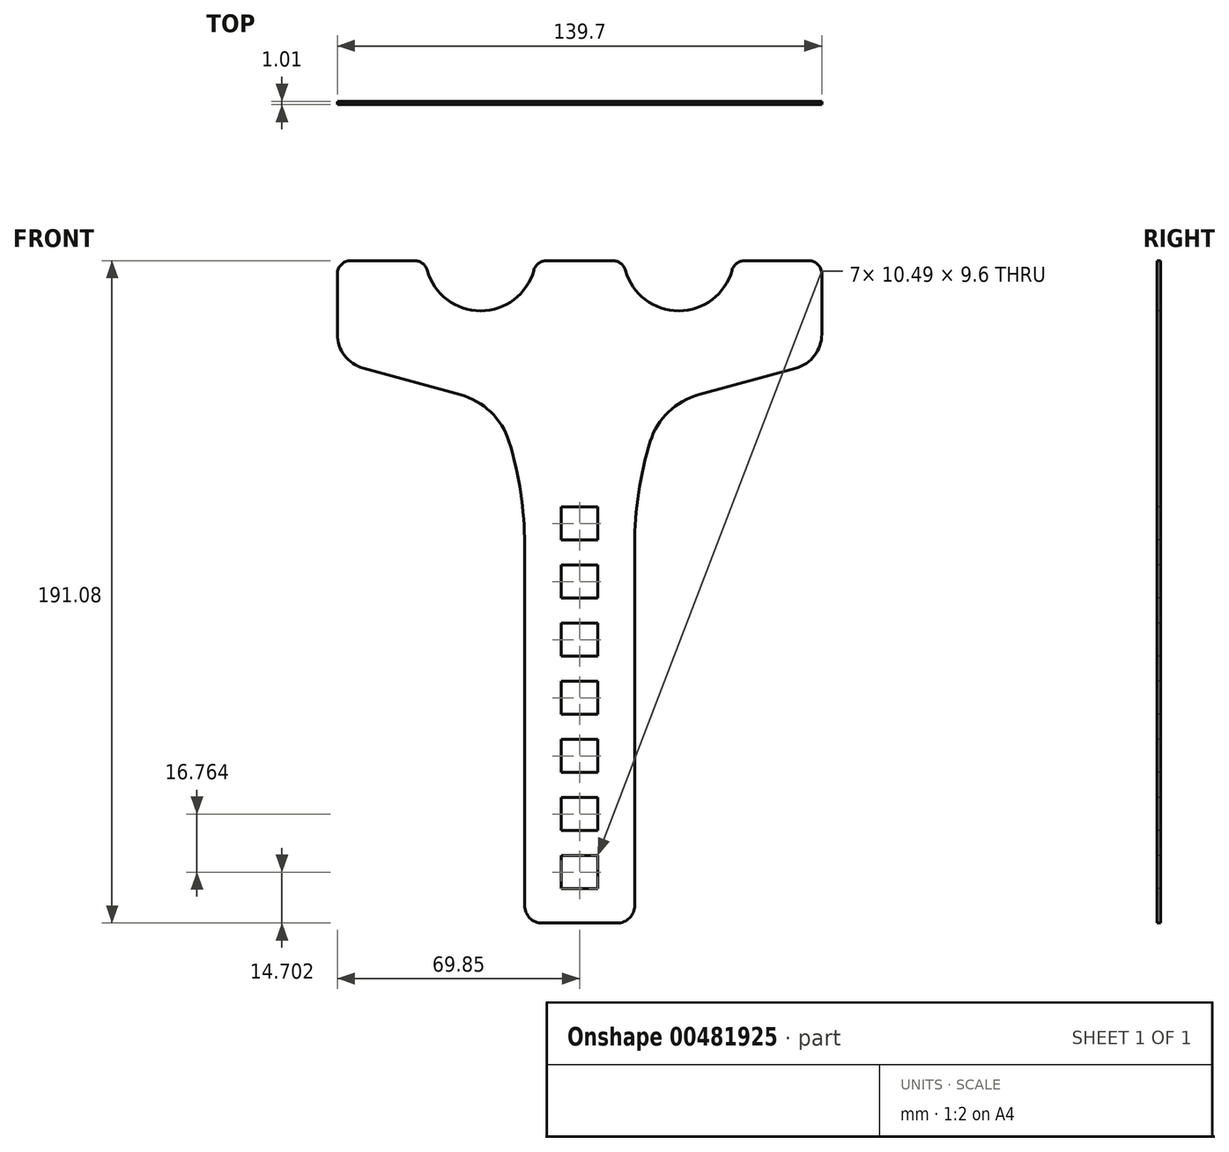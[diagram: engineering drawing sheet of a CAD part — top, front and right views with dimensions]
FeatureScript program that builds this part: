
annotation { "Feature Type Name" : "Feature", "Feature Type Description" : "" }
export const myFeature = defineFeature(function(context is Context, id is Id, definition is map)
    precondition{}
    {
        {
            var Q0;
            Q0=qCreatedBy(makeId("Front.planeOp"),FACE);
            var sketch = newSketch(context, id + "F0", { "sketchPlane" : qUnion([Q0])});
            skPoint(sketch, "E0.middle", {"position": v(0, 0) * mm});
            skLineSegment(sketch, "E1", {"start": v(-69.85, 0) * mm, "end": v(69.85, 0) * mm});
            skLineSegment(sketch, "E2", {"start": v(-69.85, 0) * mm, "end": v(-69.85, -28.96) * mm});
            skLineSegment(sketch, "E3.MirrorCS", {"start": v(69.85, 0) * mm, "end": v(69.85, -28.96) * mm});
            skPoint(sketch, "E4.middle", {"position": v(0, -50.17) * mm});
            skLineSegment(sketch, "E5", {"start": v(-69.85, -28.96) * mm, "end": v(-15.87, -28.96) * mm, "construction": true});
            skLineSegment(sketch, "E6", {"start": v(-69.85, -28.96) * mm, "end": v(-23.72, -41.59) * mm});
            skLineSegment(sketch, "E7", {"start": v(-23.72, -41.59) * mm, "end": v(-15.87, -66.22) * mm});
            skLineSegment(sketch, "E8", {"start": v(-15.87, -66.22) * mm, "end": v(-15.87, -191.08) * mm});
            skLineSegment(sketch, "E9", {"start": v(-15.87, -191.08) * mm, "end": v(0, -191.08) * mm});
            skLineSegment(sketch, "E10.MirrorCS", {"start": v(69.85, -28.96) * mm, "end": v(23.72, -41.59) * mm});
            skLineSegment(sketch, "E11.MirrorCS", {"start": v(23.72, -41.59) * mm, "end": v(15.87, -66.22) * mm});
            skLineSegment(sketch, "E12.MirrorCS", {"start": v(15.87, -66.22) * mm, "end": v(15.87, -191.08) * mm});
            skLineSegment(sketch, "E13.MirrorCS", {"start": v(15.87, -191.08) * mm, "end": v(0, -191.08) * mm});
            skLineSegment(sketch, "E14", {"start": v(-69.85, 0) * mm, "end": v(-44.45, 0) * mm, "construction": true});
            skLineSegment(sketch, "E15", {"start": v(-44.45, 0) * mm, "end": v(-12.7, 0) * mm, "construction": true});
            skLineSegment(sketch, "E16", {"start": v(-28.58, 0) * mm, "end": v(-28.58, -14.48) * mm, "construction": true});
            skArc(sketch, "E17", {"start": v(-44.45, 0) * mm, "mid": v(-28.58, -14.48) * mm, "end": v(-12.7, 0) * mm});
            skArc(sketch, "E18.MirrorCS", {"start": v(44.45, 0) * mm, "mid": v(28.58, -14.48) * mm, "end": v(12.7, 0) * mm});
            skLineSegment(sketch, "E19", {"start": v(0, 0) * mm, "end": v(0, -92.56) * mm, "construction": true});
            skLineSegment(sketch, "E20.bottom", {"start": v(5.25, -97.36) * mm, "end": v(-5.25, -97.36) * mm});
            skLineSegment(sketch, "E20.top", {"start": v(5.25, -87.76) * mm, "end": v(-5.25, -87.76) * mm});
            skLineSegment(sketch, "E20.left", {"start": v(5.25, -97.36) * mm, "end": v(5.25, -87.76) * mm});
            skLineSegment(sketch, "E20.right", {"start": v(-5.25, -97.36) * mm, "end": v(-5.25, -87.76) * mm});
            skPoint(sketch, "E20.middle", {"position": v(0, -92.56) * mm});
            skLineSegment(sketch, "E21", {"start": v(-5.25, -97.36) * mm, "end": v(-5.25, -104.52) * mm, "construction": true});
            skLineSegment(sketch, "E22", {"start": v(-5.25, -104.52) * mm, "end": v(-5.25, -114.12) * mm, "construction": true});
            skLineSegment(sketch, "E23", {"start": v(-5.25, -114.12) * mm, "end": v(-5.25, -121.29) * mm, "construction": true});
            skLineSegment(sketch, "E24", {"start": v(-5.25, -121.29) * mm, "end": v(-5.25, -130.89) * mm, "construction": true});
            skLineSegment(sketch, "E25", {"start": v(-5.25, -130.89) * mm, "end": v(-5.25, -138.05) * mm, "construction": true});
            skLineSegment(sketch, "E26", {"start": v(-5.25, -138.05) * mm, "end": v(-5.25, -147.65) * mm, "construction": true});
            skLineSegment(sketch, "E27", {"start": v(-5.25, -147.65) * mm, "end": v(-5.25, -154.81) * mm, "construction": true});
            skLineSegment(sketch, "E28", {"start": v(-5.25, -154.81) * mm, "end": v(-5.25, -164.41) * mm, "construction": true});
            skLineSegment(sketch, "E29", {"start": v(-5.25, -164.41) * mm, "end": v(-5.25, -171.58) * mm, "construction": true});
            skLineSegment(sketch, "E30", {"start": v(-5.25, -171.58) * mm, "end": v(-5.25, -181.18) * mm, "construction": true});
            skLineSegment(sketch, "E31.bottom", {"start": v(-5.25, -104.52) * mm, "end": v(5.25, -104.52) * mm});
            skLineSegment(sketch, "E31.top", {"start": v(-5.25, -114.12) * mm, "end": v(5.25, -114.12) * mm});
            skLineSegment(sketch, "E31.left", {"start": v(-5.25, -104.52) * mm, "end": v(-5.25, -114.12) * mm});
            skLineSegment(sketch, "E31.right", {"start": v(5.25, -104.52) * mm, "end": v(5.25, -114.12) * mm});
            skLineSegment(sketch, "E32.bottom", {"start": v(-5.25, -121.29) * mm, "end": v(5.25, -121.29) * mm});
            skLineSegment(sketch, "E32.top", {"start": v(-5.25, -130.89) * mm, "end": v(5.25, -130.89) * mm});
            skLineSegment(sketch, "E32.left", {"start": v(-5.25, -121.29) * mm, "end": v(-5.25, -130.89) * mm});
            skLineSegment(sketch, "E32.right", {"start": v(5.25, -121.29) * mm, "end": v(5.25, -130.89) * mm});
            skLineSegment(sketch, "E33.bottom", {"start": v(-5.25, -138.05) * mm, "end": v(5.25, -138.05) * mm});
            skLineSegment(sketch, "E33.top", {"start": v(-5.25, -147.65) * mm, "end": v(5.25, -147.65) * mm});
            skLineSegment(sketch, "E33.left", {"start": v(-5.25, -138.05) * mm, "end": v(-5.25, -147.65) * mm});
            skLineSegment(sketch, "E33.right", {"start": v(5.25, -138.05) * mm, "end": v(5.25, -147.65) * mm});
            skLineSegment(sketch, "E34.bottom", {"start": v(-5.25, -154.81) * mm, "end": v(5.25, -154.81) * mm});
            skLineSegment(sketch, "E34.top", {"start": v(-5.25, -164.41) * mm, "end": v(5.25, -164.41) * mm});
            skLineSegment(sketch, "E34.left", {"start": v(-5.25, -154.81) * mm, "end": v(-5.25, -164.41) * mm});
            skLineSegment(sketch, "E34.right", {"start": v(5.25, -154.81) * mm, "end": v(5.25, -164.41) * mm});
            skLineSegment(sketch, "E35.bottom", {"start": v(-5.25, -171.58) * mm, "end": v(5.25, -171.58) * mm});
            skLineSegment(sketch, "E35.top", {"start": v(-5.25, -181.18) * mm, "end": v(5.25, -181.18) * mm});
            skLineSegment(sketch, "E35.left", {"start": v(-5.25, -171.58) * mm, "end": v(-5.25, -181.18) * mm});
            skLineSegment(sketch, "E35.right", {"start": v(5.25, -171.58) * mm, "end": v(5.25, -181.18) * mm});
            skLineSegment(sketch, "E36", {"start": v(-5.25, -181.18) * mm, "end": v(-5.25, -97.36) * mm});
            skLineSegment(sketch, "E37", {"start": v(-5.25, -87.76) * mm, "end": v(-5.25, -80.6) * mm, "construction": true});
            skLineSegment(sketch, "E38", {"start": v(-5.25, -80.6) * mm, "end": v(-5.25, -71) * mm, "construction": true});
            skLineSegment(sketch, "E39.bottom", {"start": v(-5.25, -71) * mm, "end": v(5.25, -71) * mm});
            skLineSegment(sketch, "E39.top", {"start": v(-5.25, -80.6) * mm, "end": v(5.25, -80.6) * mm});
            skLineSegment(sketch, "E39.left", {"start": v(-5.25, -71) * mm, "end": v(-5.25, -80.6) * mm});
            skLineSegment(sketch, "E39.right", {"start": v(5.25, -71) * mm, "end": v(5.25, -80.6) * mm});
            skLineSegment(sketch, "E40", {"start": v(0, 0) * mm, "end": v(0, -19.05) * mm, "construction": true});
            skLineSegment(sketch, "E41", {"start": v(0, -19.05) * mm, "end": v(62.5, -19.05) * mm, "construction": true});
            skLineSegment(sketch, "E42", {"start": v(28.58, -14.48) * mm, "end": v(28.58, -19.05) * mm, "construction": true});
            skLineSegment(sketch, "E43", {"start": v(28.58, -19.05) * mm, "end": v(28.58, -6.35) * mm, "construction": true});
            skSolve(sketch);
        }
        {
            var Q0;
            {var subQ6=sQuery(id+"F0.wireOp",EDGE,"E2");Q0=makeQuery(id+"F0.imprint","IMPRINT",FACE,{"disambiguationData":[TD([[makeQuery(id+"F0.imprint","IMPRINT",EDGE,{"derivedFrom":subQ6}),1.0]])]});}
            extrude(context, id + "F1", {"entities" : qUnion([Q0]), "oppositeDirection" : true, "depth" : 1 * mm, "offsetDistance" : 25.4 * mm});
        }
        {
            var Q0;
            Q0=makeQuery(id+"F1.opExtrude","SWEPT_EDGE",EDGE,{"disambiguationData":[OSD([sQuery(id+"F0.wireOp",EDGE,"E6"),sQuery(id+"F0.wireOp",EDGE,"E7")])]});
            var Q1;
            Q1=makeQuery(id+"F1.opExtrude","SWEPT_EDGE",EDGE,{"disambiguationData":[OSD([sQuery(id+"F0.wireOp",EDGE,"E10.MirrorCS"),sQuery(id+"F0.wireOp",EDGE,"E11.MirrorCS")])]});
            fillet(context, id + "F2", {"entities" : qUnion([Q0, Q1]), "radius" : 20.32 * mm, "tangentPropagation" : true, "allowEdgeOverflow" : false});
        }
        {
            var Q0;
            Q0=makeQuery(id+"F1.opExtrude","SWEPT_EDGE",EDGE,{"disambiguationData":[OSD([sQuery(id+"F0.wireOp",EDGE,"E2"),sQuery(id+"F0.wireOp",EDGE,"E6")])]});
            var Q1;
            Q1=makeQuery(id+"F1.opExtrude","SWEPT_EDGE",EDGE,{"disambiguationData":[OSD([sQuery(id+"F0.wireOp",EDGE,"E3.MirrorCS"),sQuery(id+"F0.wireOp",EDGE,"E10.MirrorCS")])]});
            fillet(context, id + "F3", {"entities" : qUnion([Q0, Q1]), "radius" : 10.16 * mm, "tangentPropagation" : true, "allowEdgeOverflow" : false});
        }
        {
            var Q0;
            Q0=makeQuery(id+"F1.opExtrude","SWEPT_EDGE",EDGE,{"disambiguationData":[OSD([sQuery(id+"F0.wireOp",EDGE,"E1"),sQuery(id+"F0.wireOp",EDGE,"E3.MirrorCS")])]});
            var Q1;
            Q1=makeQuery(id+"F1.opExtrude","SWEPT_EDGE",EDGE,{"disambiguationData":[OSD([sQuery(id+"F0.wireOp",EDGE,"E1"),sQuery(id+"F0.wireOp",EDGE,"E2")])]});
            fillet(context, id + "F4", {"entities" : qUnion([Q0, Q1]), "radius" : 3.8 * mm, "tangentPropagation" : true, "allowEdgeOverflow" : false});
        }
        {
            var Q0;
            {var subQ0=sQuery(id+"F0.wireOp",EDGE,"E18.MirrorCS");var subQ1=sQuery(id+"F0.wireOp",EDGE,"E1");Q0=makeQuery(id+"F1.opExtrude","SWEPT_EDGE",EDGE,{"disambiguationData":[OSD([subQ1,subQ0]),TDD([makeQuery(id+"F0.imprint","INTERSECT",VERTEX,{"disambiguationData":[OD(1.0)],"derivedFrom":[subQ1,subQ0]})])]});}
            var Q1;
            {var subQ0=sQuery(id+"F0.wireOp",EDGE,"E17");var subQ1=sQuery(id+"F0.wireOp",EDGE,"E1");Q1=makeQuery(id+"F1.opExtrude","SWEPT_EDGE",EDGE,{"disambiguationData":[OSD([subQ1,subQ0]),TDD([makeQuery(id+"F0.imprint","INTERSECT",VERTEX,{"disambiguationData":[OD(1.0)],"derivedFrom":[subQ1,subQ0]})])]});}
            var Q2;
            {var subQ0=sQuery(id+"F0.wireOp",EDGE,"E17");var subQ1=sQuery(id+"F0.wireOp",EDGE,"E1");Q2=makeQuery(id+"F1.opExtrude","SWEPT_EDGE",EDGE,{"disambiguationData":[OSD([subQ1,subQ0]),TDD([makeQuery(id+"F0.imprint","INTERSECT",VERTEX,{"disambiguationData":[OD(0.0)],"derivedFrom":[subQ1,subQ0]})])]});}
            var Q3;
            {var subQ0=sQuery(id+"F0.wireOp",EDGE,"E18.MirrorCS");var subQ1=sQuery(id+"F0.wireOp",EDGE,"E1");Q3=makeQuery(id+"F1.opExtrude","SWEPT_EDGE",EDGE,{"disambiguationData":[OSD([subQ1,subQ0]),TDD([makeQuery(id+"F0.imprint","INTERSECT",VERTEX,{"disambiguationData":[OD(0.0)],"derivedFrom":[subQ1,subQ0]})])]});}
            fillet(context, id + "F5", {"entities" : qUnion([Q0, Q1, Q2, Q3]), "radius" : 3.8 * mm, "tangentPropagation" : true, "allowEdgeOverflow" : false});
        }
        {
            var Q0;
            Q0=makeQuery(id+"F1.opExtrude","SWEPT_EDGE",EDGE,{"disambiguationData":[OSD([sQuery(id+"F0.wireOp",EDGE,"E11.MirrorCS"),sQuery(id+"F0.wireOp",EDGE,"E12.MirrorCS")])]});
            var Q1;
            Q1=makeQuery(id+"F1.opExtrude","SWEPT_EDGE",EDGE,{"disambiguationData":[OSD([sQuery(id+"F0.wireOp",EDGE,"E7"),sQuery(id+"F0.wireOp",EDGE,"E8")])]});
            fillet(context, id + "F6", {"entities" : qUnion([Q0, Q1]), "radius" : 101.6 * mm, "tangentPropagation" : true, "allowEdgeOverflow" : false});
        }
        {
            var Q0;
            Q0=makeQuery(id+"F1.opExtrude","SWEPT_EDGE",EDGE,{"disambiguationData":[OSD([sQuery(id+"F0.wireOp",EDGE,"E12.MirrorCS"),sQuery(id+"F0.wireOp",EDGE,"E13.MirrorCS")])]});
            var Q1;
            Q1=makeQuery(id+"F1.opExtrude","SWEPT_EDGE",EDGE,{"disambiguationData":[OSD([sQuery(id+"F0.wireOp",EDGE,"E8"),sQuery(id+"F0.wireOp",EDGE,"E9")])]});
            fillet(context, id + "F7", {"entities" : qUnion([Q0, Q1]), "radius" : 5.08 * mm, "tangentPropagation" : true, "allowEdgeOverflow" : false});
        }
    });
